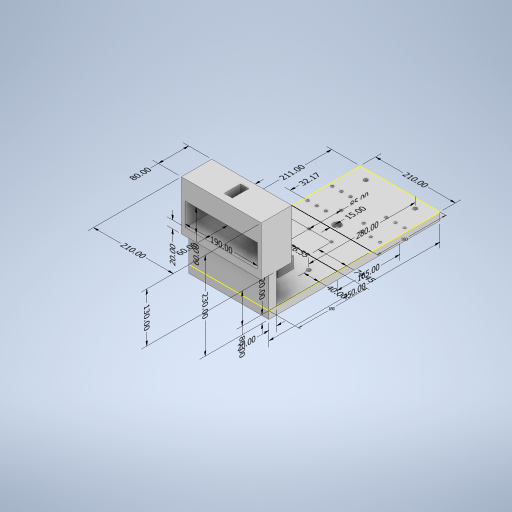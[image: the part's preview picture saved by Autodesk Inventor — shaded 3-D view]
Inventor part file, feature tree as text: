
AUTODESK INVENTOR PART (.ipt)
format: ipt  version: 2023 (Build 270158000, 158)  size: 468,480 bytes
history: native  units: mm
features: other x26, sketch x13, extrude x12, split x1
ambient origin geometry x8: Origin, YZ Plane, XZ Plane, XY Plane, X Axis, Y Axis, Z Axis, Center Point
bodies: Body1 (feature_tree)
feature tree (52):
  other  "Sólido1"
  other  "Anotaciones"
  extrude  "Extrusión1"  Depth=450.0mm
  extrude  "Extrusión2"  Depth=20.0mm
  extrude  "Extrusión3"  Depth=20.0mm
  extrude  "Extrusión4"  Depth=60.0mm
  extrude  "Extrusión5"  Depth=190.0mm
  extrude  "Extrusión6"  Depth=60.0mm TaperAngle=0.0deg
  extrude  "Extrusión7"  Depth=43.0mm
  extrude  "Extrusión8"  Depth=10.0mm
  extrude  "Extrusión9"  Depth=10.0mm
  extrude  "Extrusión10"  Depth=10.0mm
  extrude  "Extrusión11"  Depth=25.0mm
  extrude  "Extrusión12"  Depth=40.0mm
  sketch  "Boceto13"  dims[d32=40.0mm d33=40.0mm d34=40.0mm d35=43.0mm d36=0.0mm d44=20.0mm d45=10.0mm d46=0.0mm d51=7.0mm d52=7.0mm d54=7.0mm d55=20.0mm d56=0.0mm d59=20.0mm d62=20.0mm d63=0.0mm d64=20.0mm d65=30.0mm d66=30.0mm d68=74.0mm d69=31.0mm d70=84.0mm d71=41.0mm d72=10.0mm d73=0.0mm d74=84.0mm d75=41.0mm d76=30.0mm d77=0.0mm d78=7.0mm d79=68.0mm d80=80.0mm d81=7.6mm d82=10.0mm d83=7.0mm d84=30.0mm d85=0.0mm d103=180.0mm d110=180.0mm d100=9.422185mm d101=1.193524mm d102=20.0mm d104=9.135179mm d105=32.166555mm d106=5.22954mm d107=15.0mm d111=5.992022mm d112=3.930543mm d113=20.0mm d114=6.486022mm d115=31.0mm d116=1.81804mm d117=76.551816mm d118=1.179967mm d119=74.448184mm d120=85.0mm d121=5.107273mm d122=40.0mm d123=4.010082mm d124=6.491791mm d125=210.0mm d126=2.494721mm d127=7.12053mm d128=80.0mm d129=1.846859mm d130=4.658331mm d131=130.0mm d132=1.510189mm d133=8.422248mm d134=20.0mm d135=3.552555mm d136=7.273776mm d137=190.0mm d138=7.72639mm d139=2.331598mm d140=60.0mm d141=7.106272mm d142=7.779723mm d143=60.0mm d40=9.477646mm d41=4.784189mm d42=80.0mm d43=280.0mm d86=125.0mm d87=4.2098mm d88=450.0mm d89=0.666568mm d90=4.428063mm d91=230.0mm d92=6.47995mm d93=211.0mm d94=5.175864mm d95=6.811682mm d96=165.0mm d97=0.788992mm d98=0.638053mm d99=210.0mm]
  split  "Dividir1"
  sketch  "Boceto1"  dims[d0=20.0mm d1=450.0mm]
  sketch  "Boceto2"  dims[d2=210.0mm d3=0.0mm d4=20.0mm]
  sketch  "Boceto3"  dims[d5=80.0mm d6=0.0mm d7=20.0mm]
  sketch  "Boceto4"  dims[d8=210.0mm d9=60.0mm]
  sketch  "Boceto5"  dims[d10=130.0mm d11=0.0mm d12=190.0mm]
  sketch  "Boceto6"  dims[d13=60.0mm d16=60.0mm d17=0.0mm]
  sketch  "Boceto7"  dims[d18=21.0mm d19=43.0mm]
  sketch  "Boceto8"  dims[d21=43.0mm d22=0.0mm d23=10.0mm]
  sketch  "Boceto9"  dims[d24=10.0mm d25=10.0mm]
  sketch  "Boceto10"  dims[d26=10.0mm d27=165.0mm]
  sketch  "Boceto11"  dims[d28=25.0mm d29=25.0mm]
  sketch  "Boceto12"  dims[d30=165.0mm d31=40.0mm]
  other  "Cota lineal 2"
  other  "Cota lineal 3"
  other  "Cota lineal 4"
  other  "Cota lineal 5"
  other  "Cota lineal 6"
  other  "Cota lineal 7"
  other  "Cota lineal 8"
  other  "Cota lineal 9"
  other  "Cota lineal 10"
  other  "Cota lineal 11"
  other  "Cota lineal 12"
  other  "Cota lineal 13"
  other  "Cota lineal 14"
  other  "Cota lineal 15"
  other  "Cota lineal 16"
  other  "Cota lineal 17"
  other  "Cota lineal 18"
  other  "Cota lineal 19"
  other  "Cota lineal 20"
  other  "Cota lineal 21"
  other  "Cota lineal 22"
  other  "Cota lineal 23"
  other  "Cota lineal 24"
  other  "Cota lineal 25"
